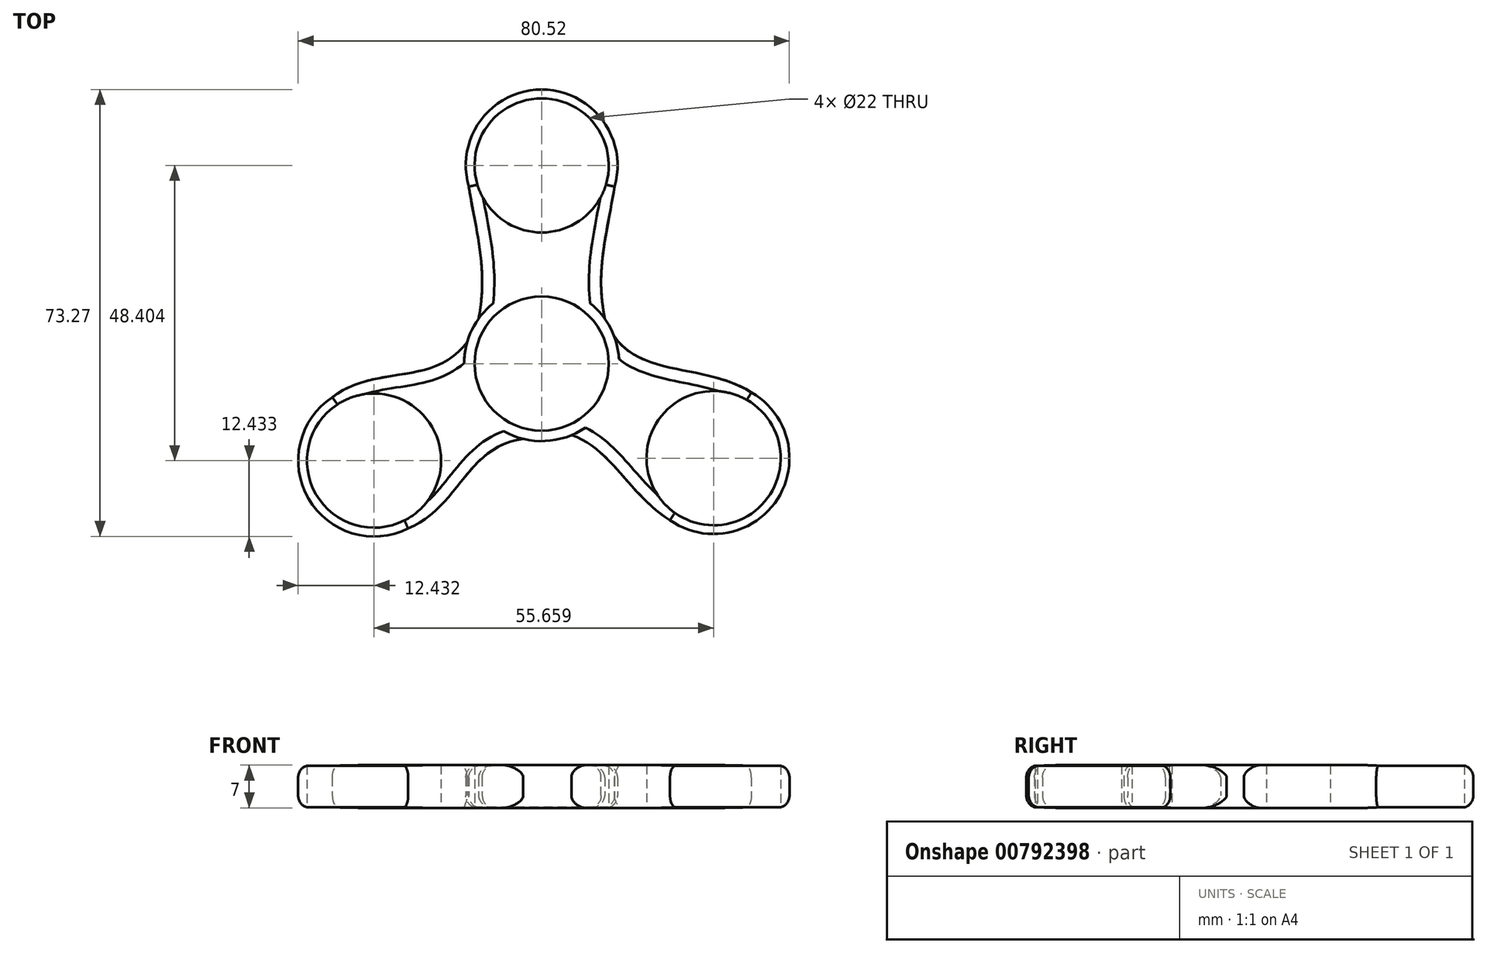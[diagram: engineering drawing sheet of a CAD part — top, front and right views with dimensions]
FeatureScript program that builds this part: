
annotation { "Feature Type Name" : "Feature", "Feature Type Description" : "" }
export const myFeature = defineFeature(function(context is Context, id is Id, definition is map)
    precondition{}
    {
        {
            var Q0;
            Q0=qCreatedBy(makeId("Top.planeOp"),FACE);
            var sketch = newSketch(context, id + "F0", { "sketchPlane" : qUnion([Q0])});
            skCircle(sketch, "E0", {"center": v(0, 0) * mm, "radius": 11 * mm});
            skCircle(sketch, "E1", {"center": v(0, 0) * mm, "radius": 12.7 * mm});
            skLineSegment(sketch, "E2", {"start": v(0, 0) * mm, "end": v(0, 40) * mm});
            skCircle(sketch, "E3", {"center": v(0, 32.5) * mm, "radius": 11 * mm});
            skCircle(sketch, "E4", {"center": v(0, 32.5) * mm, "radius": 12.43 * mm});
            skCircle(sketch, "E5.1.0", {"center": v(-27.48, -15.9) * mm, "radius": 12.43 * mm});
            skCircle(sketch, "E5.1.1", {"center": v(-27.48, -15.9) * mm, "radius": 11 * mm});
            skCircle(sketch, "E5.2.0", {"center": v(28.18, -15.5) * mm, "radius": 12.43 * mm});
            skCircle(sketch, "E5.2.1", {"center": v(28.18, -15.5) * mm, "radius": 11 * mm});
            skPoint(sketch, "E5.center", {"position": v(0.23, 0.37) * mm});
            skLineSegment(sketch, "E6.1.1", {"start": v(0.38, 0.22) * mm, "end": v(-34.24, -19.8) * mm});
            skLineSegment(sketch, "E6.2.1", {"start": v(0.63, 0.44) * mm, "end": v(35.28, -19.56) * mm});
            skPoint(sketch, "E6.center", {"position": v(0.45, 0.04) * mm});
            skLineSegment(sketch, "E7", {"start": v(2.24, -12.15) * mm, "end": v(11.87, 4.52) * mm});
            skFitSpline(sketch, "E8", {"points": [v(-12.43, 32.93) * mm, v(-10.36, 7.35) * mm], "startDerivative": vector(2.64, -28.6) * mm, "endDerivative": vector(-5.71, -28.64) * mm});
            skFitSpline(sketch, "E9.MirrorCS", {"points": [v(12.43, 32.93) * mm, v(10.36, 7.35) * mm], "startDerivative": vector(-2.64, -28.6) * mm, "endDerivative": vector(5.71, -28.64) * mm});
            skFitSpline(sketch, "E10", {"points": [v(11.87, 4.52) * mm, v(34.38, -4.71) * mm], "startDerivative": vector(13.47, -20.13) * mm, "endDerivative": vector(22.23, -14.13) * mm});
            skFitSpline(sketch, "E11.MirrorCS", {"points": [v(2.72, -11.32) * mm, v(21.97, -26.2) * mm], "startDerivative": vector(24.17, -1.6) * mm, "endDerivative": vector(23.36, -12.19) * mm});
            skFitSpline(sketch, "E12", {"points": [v(-12.2, 3.51) * mm, v(-34.32, -5.51) * mm], "startDerivative": vector(-17.22, -22.32) * mm, "endDerivative": vector(-21.4, -16.54) * mm});
            skFitSpline(sketch, "E13.MirrorCS", {"points": [v(-3.04, -12.33) * mm, v(-21.89, -27) * mm], "startDerivative": vector(-27.93, -3.8) * mm, "endDerivative": vector(-25.01, -10.3) * mm});
            skSolve(sketch);
        }
        {
            var Q0;
            Q0 = qSketchRegion(id + "F0", true);
            extrude(context, id + "F1", {"entities" : qUnion([Q0]), "depth" : 7 * mm, "offsetDistance" : 25.4 * mm});
        }
        {
            var Q0;
            Q0=makeQuery(id+"F1.opExtrude","CAP_EDGE",EDGE,{"disambiguationData":[OSD([sQuery(id+"F0.wireOp",EDGE,"E12")])],"isStart":false});
            var Q1;
            Q1=makeQuery(id+"F1.opExtrude","CAP_EDGE",EDGE,{"disambiguationData":[OSD([sQuery(id+"F0.wireOp",EDGE,"E5.1.0")])],"isStart":false});
            var Q2;
            Q2=makeQuery(id+"F1.opExtrude","CAP_EDGE",EDGE,{"disambiguationData":[OSD([sQuery(id+"F0.wireOp",EDGE,"E11.MirrorCS")])],"isStart":false});
            var Q3;
            Q3=makeQuery(id+"F1.opExtrude","CAP_EDGE",EDGE,{"disambiguationData":[OSD([sQuery(id+"F0.wireOp",EDGE,"E5.2.0")])],"isStart":false});
            var Q4;
            Q4=makeQuery(id+"F1.opExtrude","CAP_EDGE",EDGE,{"disambiguationData":[OSD([sQuery(id+"F0.wireOp",EDGE,"E9.MirrorCS")])],"isStart":false});
            var Q5;
            Q5=makeQuery(id+"F1.opExtrude","CAP_EDGE",EDGE,{"disambiguationData":[OSD([sQuery(id+"F0.wireOp",EDGE,"E8")])],"isStart":false});
            var Q6;
            Q6=makeQuery(id+"F1.opExtrude","CAP_EDGE",EDGE,{"disambiguationData":[OSD([sQuery(id+"F0.wireOp",EDGE,"E4")])],"isStart":false});
            fillet(context, id + "F2", {"entities" : qUnion([Q0, Q1, Q2, Q3, Q4, Q5, Q6]), "radius" : 2 * mm, "tangentPropagation" : true, "allowEdgeOverflow" : false});
        }
        {
            var Q0;
            Q0=makeQuery(id+"F1.opExtrude","CAP_EDGE",EDGE,{"disambiguationData":[OSD([sQuery(id+"F0.wireOp",EDGE,"E12")])],"isStart":true});
            var Q1;
            Q1=makeQuery(id+"F1.opExtrude","CAP_EDGE",EDGE,{"disambiguationData":[OSD([sQuery(id+"F0.wireOp",EDGE,"E5.1.0")])],"isStart":true});
            var Q2;
            Q2=makeQuery(id+"F1.opExtrude","CAP_EDGE",EDGE,{"disambiguationData":[OSD([sQuery(id+"F0.wireOp",EDGE,"E13.MirrorCS")])],"isStart":true});
            var Q3;
            Q3=makeQuery(id+"F1.opExtrude","CAP_EDGE",EDGE,{"disambiguationData":[OSD([sQuery(id+"F0.wireOp",EDGE,"E11.MirrorCS")])],"isStart":true});
            var Q4;
            Q4=makeQuery(id+"F1.opExtrude","CAP_EDGE",EDGE,{"disambiguationData":[OSD([sQuery(id+"F0.wireOp",EDGE,"E5.2.0")])],"isStart":true});
            var Q5;
            Q5=makeQuery(id+"F1.opExtrude","CAP_EDGE",EDGE,{"disambiguationData":[OSD([sQuery(id+"F0.wireOp",EDGE,"E9.MirrorCS")])],"isStart":true});
            var Q6;
            Q6=makeQuery(id+"F1.opExtrude","CAP_EDGE",EDGE,{"disambiguationData":[OSD([sQuery(id+"F0.wireOp",EDGE,"E8")])],"isStart":true});
            var Q7;
            Q7=makeQuery(id+"F1.opExtrude","CAP_EDGE",EDGE,{"disambiguationData":[OSD([sQuery(id+"F0.wireOp",EDGE,"E4")])],"isStart":true});
            fillet(context, id + "F3", {"entities" : qUnion([Q0, Q1, Q2, Q3, Q4, Q5, Q6, Q7]), "radius" : 2 * mm, "tangentPropagation" : true, "allowEdgeOverflow" : false});
        }
    });
